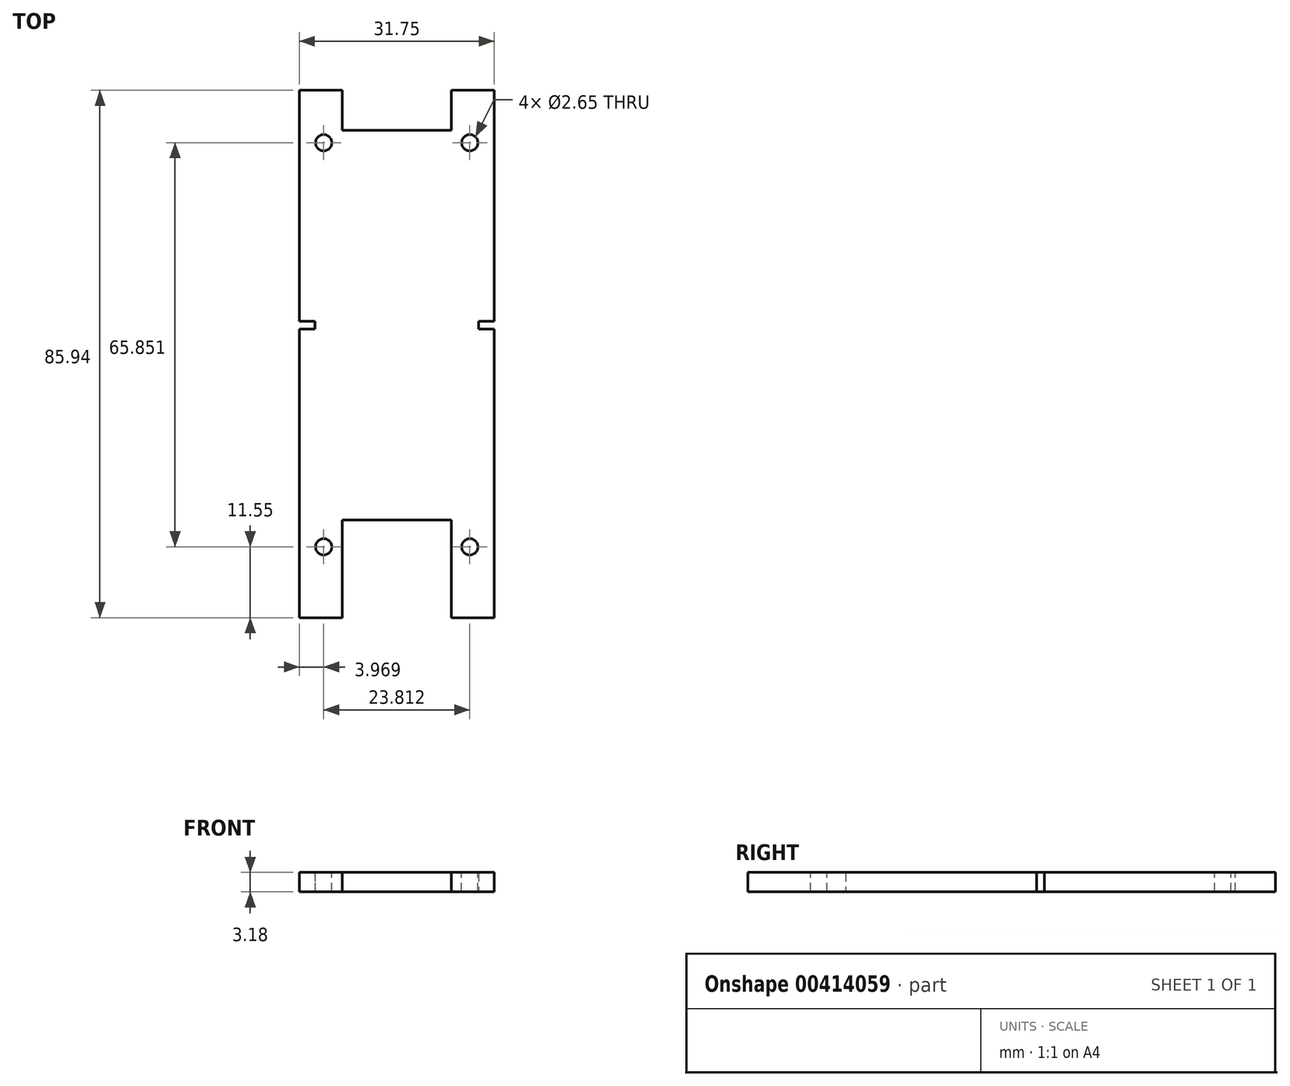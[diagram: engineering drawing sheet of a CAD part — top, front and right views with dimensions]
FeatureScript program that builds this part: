
annotation { "Feature Type Name" : "Feature", "Feature Type Description" : "" }
export const myFeature = defineFeature(function(context is Context, id is Id, definition is map)
    precondition{}
    {
        {
            var Q0;
            Q0=qCreatedBy(makeId("Top.planeOp"),FACE);
            var sketch = newSketch(context, id + "F0", { "sketchPlane" : qUnion([Q0])});
            skLineSegment(sketch, "E0.bottom", {"start": v(0, 0) * mm, "end": v(31.75, 0) * mm});
            skLineSegment(sketch, "E0.top", {"start": v(0, 63.5) * mm, "end": v(31.75, 63.5) * mm});
            skLineSegment(sketch, "E0.left", {"start": v(0, 0) * mm, "end": v(0, 63.5) * mm});
            skLineSegment(sketch, "E0.right", {"start": v(31.75, 0) * mm, "end": v(31.75, 63.5) * mm});
            skSolve(sketch);
        }
        {
            var Q0;
            Q0=makeQuery(id+"F0.imprint","IMPRINT",FACE,{"disambiguationData":[TD([[makeQuery(id+"F0.imprint","IMPRINT",EDGE,{"derivedFrom":sQuery(id+"F0.wireOp",EDGE,"E0.bottom")}),1.0]])]});
            extrude(context, id + "F1", {"entities" : qUnion([Q0]), "depth" : 3.17 * mm});
        }
        {
            var Q0;
            Q0=makeQuery(id+"F1.opExtrude","SWEPT_FACE",FACE,{"disambiguationData":[OSD([sQuery(id+"F0.wireOp",EDGE,"E0.right")])]});
            var sketch = newSketch(context, id + "F2", { "sketchPlane" : qUnion([Q0])});
            skLineSegment(sketch, "E1.bottom", {"start": v(32.38, 3.18) * mm, "end": v(31.12, 3.18) * mm});
            skLineSegment(sketch, "E1.top", {"start": v(32.38, 0) * mm, "end": v(31.12, 0) * mm});
            skLineSegment(sketch, "E1.left", {"start": v(32.38, 3.18) * mm, "end": v(32.38, 0) * mm});
            skLineSegment(sketch, "E1.right", {"start": v(31.12, 3.18) * mm, "end": v(31.12, 0) * mm});
            skPoint(sketch, "E1.middle", {"position": v(31.75, 1.59) * mm});
            skPoint(sketch, "E2.orphan", {"position": v(31.75, 3.18) * mm});
            skPoint(sketch, "E3.end.orphan", {"position": v(31.75, 0) * mm});
            skSolve(sketch);
        }
        {
            var Q0;
            Q0=makeQuery(id+"F2.imprint","IMPRINT",FACE,{"disambiguationData":[TD([[makeQuery(id+"F2.imprint","IMPRINT",EDGE,{"derivedFrom":sQuery(id+"F2.wireOp",EDGE,"E1.bottom")}),-1.0]])]});
            extrude(context, id + "F3", {"entities" : qUnion([Q0]), "operationType" : NewBodyOperationType.REMOVE, "oppositeDirection" : true, "depth" : 2.54 * mm});
        }
        {
            var Q0;
            Q0=makeQuery(id+"F1.opExtrude","SWEPT_FACE",FACE,{"disambiguationData":[OSD([sQuery(id+"F0.wireOp",EDGE,"E0.left")])]});
            var sketch = newSketch(context, id + "F4", { "sketchPlane" : qUnion([Q0])});
            skLineSegment(sketch, "E4.bottom", {"start": v(-31.11, 3.18) * mm, "end": v(-32.38, 3.18) * mm});
            skLineSegment(sketch, "E4.top", {"start": v(-31.11, 0) * mm, "end": v(-32.38, 0) * mm});
            skLineSegment(sketch, "E4.left", {"start": v(-31.11, 3.18) * mm, "end": v(-31.11, 0) * mm});
            skLineSegment(sketch, "E4.right", {"start": v(-32.38, 3.18) * mm, "end": v(-32.38, 0) * mm});
            skPoint(sketch, "E4.middle", {"position": v(-31.75, 1.59) * mm});
            skPoint(sketch, "E5.orphan", {"position": v(-31.75, 3.18) * mm});
            skPoint(sketch, "E6.end.orphan", {"position": v(-31.75, 0) * mm});
            skSolve(sketch);
        }
        {
            var Q0;
            Q0=makeQuery(id+"F4.imprint","IMPRINT",FACE,{"disambiguationData":[TD([[makeQuery(id+"F4.imprint","IMPRINT",EDGE,{"derivedFrom":sQuery(id+"F4.wireOp",EDGE,"E4.bottom")}),1.0]])]});
            extrude(context, id + "F5", {"entities" : qUnion([Q0]), "operationType" : NewBodyOperationType.REMOVE, "oppositeDirection" : true, "depth" : 2.54 * mm});
        }
        {
            var Q0;
            Q0=makeQuery(id+"F1.opExtrude","SWEPT_FACE",FACE,{"disambiguationData":[OSD([sQuery(id+"F0.wireOp",EDGE,"E0.bottom")])]});
            var sketch = newSketch(context, id + "F6", { "sketchPlane" : qUnion([Q0])});
            skLineSegment(sketch, "E7", {"start": v(15.87, 3.18) * mm, "end": v(15.87, 0) * mm});
            skLineSegment(sketch, "E8.bottom", {"start": v(24.76, 3.18) * mm, "end": v(6.98, 3.18) * mm});
            skLineSegment(sketch, "E8.top", {"start": v(24.76, 0) * mm, "end": v(6.98, 0) * mm});
            skLineSegment(sketch, "E8.left", {"start": v(24.76, 3.18) * mm, "end": v(24.76, 0) * mm});
            skLineSegment(sketch, "E8.right", {"start": v(6.98, 3.18) * mm, "end": v(6.98, 0) * mm});
            skPoint(sketch, "E8.middle", {"position": v(15.87, 1.59) * mm});
            skSolve(sketch);
        }
        {
            var Q0;
            {var subQ0=sQuery(id+"F6.wireOp",EDGE,"E8.right");Q0=makeQuery(id+"F6.imprint","IMPRINT",FACE,{"disambiguationData":[TD([[makeQuery(id+"F6.imprint","IMPRINT",EDGE,{"derivedFrom":subQ0}),-1.0]])]});}
            var Q1;
            {var subQ0=sQuery(id+"F6.wireOp",EDGE,"E8.left");Q1=makeQuery(id+"F6.imprint","IMPRINT",FACE,{"disambiguationData":[TD([[makeQuery(id+"F6.imprint","IMPRINT",EDGE,{"derivedFrom":subQ0}),1.0]])]});}
            extrude(context, id + "F7", {"entities" : qUnion([Q0, Q1]), "operationType" : NewBodyOperationType.ADD, "depth" : 6.35 * mm});
        }
        {
            var Q0;
            {var subQ0=sQuery(id+"F0.wireOp",EDGE,"E0.bottom");var subQ1=makeQuery(id+"F1.opExtrude","CAP_EDGE",EDGE,{"disambiguationData":[OSD([subQ0])],"isStart":false});var subQ2=sQuery(id+"F0.wireOp",EDGE,"E0.right");var subQ4=sQuery(id+"F0.wireOp",EDGE,"E0.left");Q0=makeQuery(id+"F7.boolean.opBoolean","MERGE",FACE,{"derivedFrom":[makeQuery(id+"F1.opExtrude","CAP_FACE",FACE,{"disambiguationData":[OSD([subQ0,sQuery(id+"F0.wireOp",EDGE,"E0.top"),subQ4,subQ2])],"isStart":false}),makeQuery(id+"F7.opExtrude","SWEPT_FACE",FACE,{"disambiguationData":[OSD([subQ0]),TDD([makeQuery(id+"F6.imprint","IMPRINT",EDGE,{"disambiguationData":[TD([[makeQuery(id+"F6.imprint","INTERSECT",VERTEX,{"derivedFrom":[makeQuery(id+"F1.opExtrude","SWEPT_EDGE",EDGE,{"disambiguationData":[OSD([subQ0,subQ4])]}),subQ1]}),-1.0]])],"derivedFrom":subQ1})])]}),makeQuery(id+"F7.opExtrude","SWEPT_FACE",FACE,{"disambiguationData":[OSD([subQ0]),TDD([makeQuery(id+"F6.imprint","IMPRINT",EDGE,{"disambiguationData":[TD([[makeQuery(id+"F6.imprint","INTERSECT",VERTEX,{"derivedFrom":[makeQuery(id+"F1.opExtrude","SWEPT_EDGE",EDGE,{"disambiguationData":[OSD([subQ0,subQ2])]}),subQ1]}),1.0]])],"derivedFrom":subQ1})])]})]});}
            var sketch = newSketch(context, id + "F8", { "sketchPlane" : qUnion([Q0])});
            skLineSegment(sketch, "E9", {"start": v(3.97, -6.35) * mm, "end": v(3.97, -4.35) * mm});
            skLineSegment(sketch, "E10", {"start": v(3.97, -4.35) * mm, "end": v(27.78, -4.35) * mm});
            skLineSegment(sketch, "E11", {"start": v(27.78, -4.35) * mm, "end": v(27.78, -6.35) * mm});
            skPoint(sketch, "E12.end.orphan", {"position": v(3.5, 0) * mm});
            skPoint(sketch, "E12.start.orphan", {"position": v(3.5, -6.35) * mm});
            skPoint(sketch, "E13.end.orphan", {"position": v(28.26, 0) * mm});
            skPoint(sketch, "E13.start.orphan", {"position": v(28.26, -6.35) * mm});
            skLineSegment(sketch, "E14", {"start": v(15.87, 0) * mm, "end": v(15.87, -4.35) * mm});
            skCircle(sketch, "E15", {"center": v(3.97, -4.35) * mm, "radius": 1.32 * mm});
            skCircle(sketch, "E16", {"center": v(27.78, -4.35) * mm, "radius": 1.32 * mm});
            skLineSegment(sketch, "E17.bottom", {"start": v(3.97, 63.5) * mm, "end": v(27.78, 63.5) * mm});
            skLineSegment(sketch, "E17.top", {"start": v(3.97, 61.5) * mm, "end": v(27.78, 61.5) * mm});
            skLineSegment(sketch, "E17.left", {"start": v(3.97, 63.5) * mm, "end": v(3.97, 62.83) * mm});
            skLineSegment(sketch, "E17.right", {"start": v(27.78, 63.5) * mm, "end": v(27.78, 62.83) * mm});
            skPoint(sketch, "E18", {"position": v(15.87, 61.5) * mm});
            skLineSegment(sketch, "E19", {"start": v(15.87, 61.5) * mm, "end": v(15.87, 0) * mm});
            skCircle(sketch, "E20", {"center": v(3.97, 61.5) * mm, "radius": 1.32 * mm});
            skCircle(sketch, "E21", {"center": v(27.78, 61.5) * mm, "radius": 1.32 * mm});
            skSolve(sketch);
        }
        {
            var Q0;
            {var subQ0=sQuery(id+"F8.wireOp",EDGE,"E10");var subQ1=sQuery(id+"F8.wireOp",EDGE,"E9");var subQ2=makeQuery(id+"F8.imprint","INTERSECT",VERTEX,{"derivedFrom":[subQ1,subQ0]});Q0=makeQuery(id+"F8.imprint","IMPRINT",FACE,{"disambiguationData":[TD([[makeQuery(id+"F8.imprint","IMPRINT",EDGE,{"disambiguationData":[TD([[subQ2,1.0]])],"derivedFrom":subQ1}),1.0]])]});}
            var Q1;
            {var subQ0=sQuery(id+"F8.wireOp",EDGE,"E10");var subQ1=sQuery(id+"F8.wireOp",EDGE,"E9");var subQ2=makeQuery(id+"F8.imprint","INTERSECT",VERTEX,{"derivedFrom":[subQ1,subQ0]});Q1=makeQuery(id+"F8.imprint","IMPRINT",FACE,{"disambiguationData":[TD([[makeQuery(id+"F8.imprint","IMPRINT",EDGE,{"disambiguationData":[TD([[subQ2,1.0]])],"derivedFrom":subQ1}),-1.0]])]});}
            var Q2;
            {var subQ0=sQuery(id+"F8.wireOp",EDGE,"E11");var subQ1=sQuery(id+"F8.wireOp",EDGE,"E10");var subQ2=makeQuery(id+"F8.imprint","INTERSECT",VERTEX,{"derivedFrom":[subQ1,subQ0]});Q2=makeQuery(id+"F8.imprint","IMPRINT",FACE,{"disambiguationData":[TD([[makeQuery(id+"F8.imprint","IMPRINT",EDGE,{"disambiguationData":[TD([[subQ2,1.0]])],"derivedFrom":subQ1}),1.0]])]});}
            var Q3;
            {var subQ0=sQuery(id+"F8.wireOp",EDGE,"E11");var subQ1=sQuery(id+"F8.wireOp",EDGE,"E10");var subQ2=makeQuery(id+"F8.imprint","INTERSECT",VERTEX,{"derivedFrom":[subQ1,subQ0]});Q3=makeQuery(id+"F8.imprint","IMPRINT",FACE,{"disambiguationData":[TD([[makeQuery(id+"F8.imprint","IMPRINT",EDGE,{"disambiguationData":[TD([[subQ2,1.0]])],"derivedFrom":subQ1}),-1.0]])]});}
            extrude(context, id + "F9", {"entities" : qUnion([Q0, Q1, Q2, Q3]), "operationType" : NewBodyOperationType.REMOVE, "oppositeDirection" : true, "depth" : 25.4 * mm});
        }
        {
            var Q0;
            {var subQ0=sQuery(id+"F8.wireOp",EDGE,"E20");var subQ1=makeQuery(id+"F8.imprint","INTERSECT",VERTEX,{"derivedFrom":[sQuery(id+"F8.wireOp",EDGE,"E17.left"),subQ0]});Q0=makeQuery(id+"F8.imprint","IMPRINT",FACE,{"disambiguationData":[TD([[makeQuery(id+"F8.imprint","IMPRINT",EDGE,{"disambiguationData":[TD([[subQ1,1.0]])],"derivedFrom":subQ0}),1.0]])]});}
            var Q1;
            {var subQ0=sQuery(id+"F8.wireOp",EDGE,"E21");var subQ1=makeQuery(id+"F8.imprint","INTERSECT",VERTEX,{"derivedFrom":[sQuery(id+"F8.wireOp",EDGE,"E17.right"),subQ0]});Q1=makeQuery(id+"F8.imprint","IMPRINT",FACE,{"disambiguationData":[TD([[makeQuery(id+"F8.imprint","IMPRINT",EDGE,{"disambiguationData":[TD([[subQ1,-1.0]])],"derivedFrom":subQ0}),1.0]])]});}
            extrude(context, id + "F10", {"entities" : qUnion([Q0, Q1]), "operationType" : NewBodyOperationType.REMOVE, "oppositeDirection" : true, "depth" : 25.4 * mm});
        }
        {
            var Q0;
            Q0=makeQuery(id+"F1.opExtrude","SWEPT_FACE",FACE,{"disambiguationData":[OSD([sQuery(id+"F0.wireOp",EDGE,"E0.top")])]});
            var sketch = newSketch(context, id + "F11", { "sketchPlane" : qUnion([Q0])});
            skLineSegment(sketch, "E22", {"start": v(-15.87, 3.18) * mm, "end": v(-15.87, 0) * mm});
            skLineSegment(sketch, "E23.bottom", {"start": v(-24.76, 0) * mm, "end": v(-6.98, 0) * mm});
            skLineSegment(sketch, "E23.top", {"start": v(-24.76, 3.18) * mm, "end": v(-6.98, 3.18) * mm});
            skLineSegment(sketch, "E23.left", {"start": v(-24.76, 0) * mm, "end": v(-24.76, 3.17) * mm});
            skLineSegment(sketch, "E23.right", {"start": v(-6.98, 0) * mm, "end": v(-6.98, 3.17) * mm});
            skPoint(sketch, "E23.middle", {"position": v(-15.87, 1.59) * mm});
            skSolve(sketch);
        }
        {
            var Q0;
            Q0=makeQuery(id+"F7.opExtrude","CAP_FACE",FACE,{"disambiguationData":[OSD([sQuery(id+"F0.wireOp",EDGE,"E0.bottom"),sQuery(id+"F0.wireOp",EDGE,"E0.right"),sQuery(id+"F6.wireOp",EDGE,"E8.left")])],"isStart":false});
            var Q1;
            Q1=makeQuery(id+"F7.opExtrude","CAP_FACE",FACE,{"disambiguationData":[OSD([sQuery(id+"F0.wireOp",EDGE,"E0.bottom"),sQuery(id+"F0.wireOp",EDGE,"E0.left"),sQuery(id+"F6.wireOp",EDGE,"E8.right")])],"isStart":false});
            extrude(context, id + "F12", {"entities" : qUnion([Q0, Q1]), "operationType" : NewBodyOperationType.ADD, "depth" : 9.55 * mm});
        }
        {
            var Q0;
            {var subQ0=sQuery(id+"F11.wireOp",EDGE,"E23.left");Q0=makeQuery(id+"F11.imprint","IMPRINT",FACE,{"disambiguationData":[TD([[makeQuery(id+"F11.imprint","IMPRINT",EDGE,{"derivedFrom":subQ0}),1.0]])]});}
            var Q1;
            {var subQ0=sQuery(id+"F11.wireOp",EDGE,"E23.right");Q1=makeQuery(id+"F11.imprint","IMPRINT",FACE,{"disambiguationData":[TD([[makeQuery(id+"F11.imprint","IMPRINT",EDGE,{"derivedFrom":subQ0}),-1.0]])]});}
            extrude(context, id + "F13", {"entities" : qUnion([Q0, Q1]), "operationType" : NewBodyOperationType.ADD, "depth" : 6.54 * mm});
        }
    });
